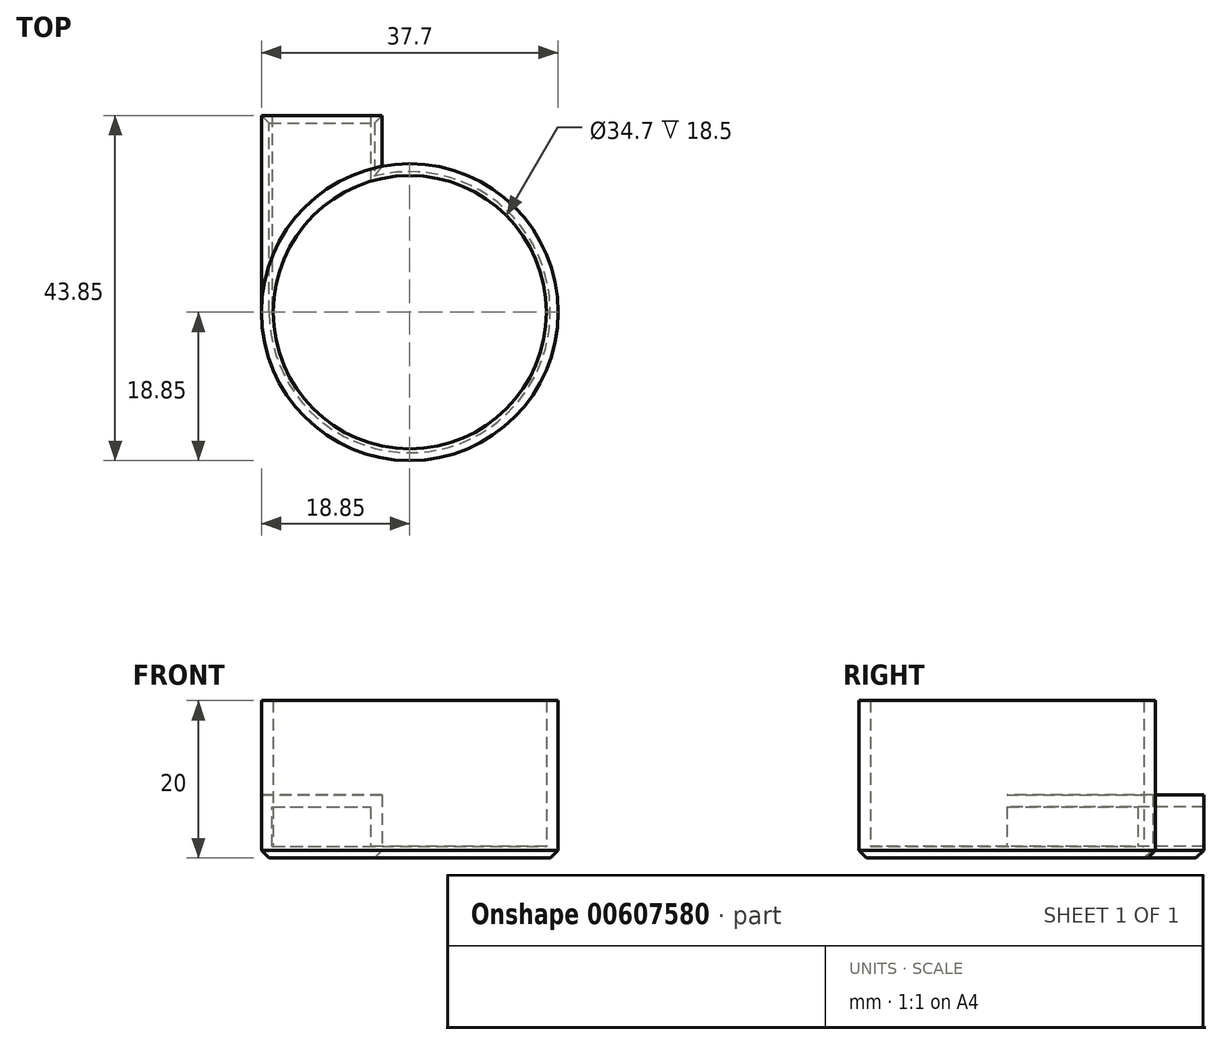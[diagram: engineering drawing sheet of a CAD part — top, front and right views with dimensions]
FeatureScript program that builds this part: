
annotation { "Feature Type Name" : "Feature", "Feature Type Description" : "" }
export const myFeature = defineFeature(function(context is Context, id is Id, definition is map)
    precondition{}
    {
        {
            var Q0;
            Q0=qCreatedBy(makeId("Top.planeOp"),FACE);
            var sketch = newSketch(context, id + "F0", { "sketchPlane" : qUnion([Q0])});
            skCircle(sketch, "E0", {"center": v(0, 0) * mm, "radius": 17.35 * mm});
            skCircle(sketch, "E1.0", {"center": v(0, 0) * mm, "radius": 18.85 * mm});
            skSolve(sketch);
        }
        {
            var Q0;
            Q0=makeQuery(id+"F0.imprint","IMPRINT",FACE,{"disambiguationData":[TD([[makeQuery(id+"F0.imprint","IMPRINT",EDGE,{"derivedFrom":sQuery(id+"F0.wireOp",EDGE,"E0")}),1.0]])]});
            extrude(context, id + "F1", {"entities" : qUnion([Q0]), "depth" : 1.5 * mm, "offsetDistance" : 25 * mm});
        }
        {
            var Q0;
            Q0=makeQuery(id+"F0.imprint","IMPRINT",FACE,{"disambiguationData":[TD([[makeQuery(id+"F0.imprint","IMPRINT",EDGE,{"derivedFrom":sQuery(id+"F0.wireOp",EDGE,"E0")}),-1.0]])]});
            extrude(context, id + "F2", {"entities" : qUnion([Q0]), "operationType" : NewBodyOperationType.ADD, "depth" : 20 * mm, "offsetDistance" : 25 * mm});
        }
        {
            var Q0;
            Q0=qCreatedBy(makeId("Front.planeOp"),FACE);
            var sketch = newSketch(context, id + "F3", { "sketchPlane" : qUnion([Q0])});
            skLineSegment(sketch, "E2.bottom", {"start": v(-17.5, 1.5) * mm, "end": v(-5, 1.5) * mm});
            skLineSegment(sketch, "E2.top", {"start": v(-17.5, 6.5) * mm, "end": v(-5, 6.5) * mm});
            skLineSegment(sketch, "E2.left", {"start": v(-17.5, 1.5) * mm, "end": v(-17.5, 6.5) * mm});
            skLineSegment(sketch, "E3", {"start": v(-5, 6.5) * mm, "end": v(-5, 1.5) * mm});
            skPoint(sketch, "E2.right.end.orphan", {"position": v(0, 6.5) * mm});
            skSolve(sketch);
        }
        {
            var Q0;
            Q0 = qSketchRegion(id + "F3", true);
            extrude(context, id + "F4", {"entities" : qUnion([Q0]), "operationType" : NewBodyOperationType.REMOVE, "oppositeDirection" : true, "depth" : 25 * mm, "offsetDistance" : 25 * mm});
        }
        {
            var Q0;
            Q0=qCreatedBy(makeId("Front.planeOp"),FACE);
            cPlane(context, id + "F5", {"entities" : qUnion([Q0]), "cplaneType" : CPlaneType.OFFSET, "offset" : 25 * mm, "oppositeDirection" : true, "width" : 150 * mm, "height" : 150 * mm});
        }
        {
            var Q0;
            Q0=qCreatedBy(id+"F5.planeOp",FACE);
            var sketch = newSketch(context, id + "F6", { "sketchPlane" : qUnion([Q0])});
            skLineSegment(sketch, "E4.bottom", {"start": v(-17.5, 1.5) * mm, "end": v(-5, 1.5) * mm});
            skLineSegment(sketch, "E4.top", {"start": v(-17.5, 6.5) * mm, "end": v(-5, 6.5) * mm});
            skLineSegment(sketch, "E4.left", {"start": v(-17.5, 1.5) * mm, "end": v(-17.5, 6.5) * mm});
            skLineSegment(sketch, "E5", {"start": v(-5, 6.5) * mm, "end": v(-5, 1.5) * mm});
            skPoint(sketch, "E4.right.end.orphan", {"position": v(9, 6.5) * mm});
            skLineSegment(sketch, "E6.0", {"start": v(-3.5, 8) * mm, "end": v(-3.5, 0) * mm});
            skLineSegment(sketch, "E6.1", {"start": v(-18.85, 8) * mm, "end": v(-3.5, 8) * mm});
            skLineSegment(sketch, "E6.3", {"start": v(-19, 0) * mm, "end": v(-3.5, 0) * mm});
            skLineSegment(sketch, "E7", {"start": v(-18.85, 0) * mm, "end": v(-18.85, 8) * mm});
            skPoint(sketch, "E6.2.end.orphan", {"position": v(-19, 8) * mm});
            skSolve(sketch);
        }
        {
            var Q0;
            Q0=makeQuery(id+"F6.imprint","IMPRINT",FACE,{"disambiguationData":[TD([[makeQuery(id+"F6.imprint","IMPRINT",EDGE,{"derivedFrom":sQuery(id+"F6.wireOp",EDGE,"E4.bottom")}),-1.0]])]});
            var Q1;
            Q1=makeQuery(id+"F2.opExtrude","SWEPT_FACE",FACE,{"disambiguationData":[OSD([sQuery(id+"F0.wireOp",EDGE,"E1.0")])]});
            extrude(context, id + "F7", {"entities" : qUnion([Q0]), "operationType" : NewBodyOperationType.ADD, "endBound" : BoundingType.UP_TO_SURFACE, "depth" : 25 * mm, "endBoundEntityFace" : qUnion([Q1]), "offsetDistance" : 25 * mm});
        }
        {
            var Q0;
            {var subQ0=sQuery(id+"F0.wireOp",EDGE,"E0");Q0=makeQuery(id+"F7.boolean.opBoolean","MERGE",FACE,{"derivedFrom":[makeQuery(id+"F2.boolean.opBoolean","MERGE",FACE,{"derivedFrom":[makeQuery(id+"F1.opExtrude","CAP_FACE",FACE,{"disambiguationData":[OSD([subQ0])],"isStart":true}),makeQuery(id+"F2.opExtrude","CAP_FACE",FACE,{"disambiguationData":[OSD([subQ0,sQuery(id+"F0.wireOp",EDGE,"E1.0")])],"isStart":true})]}),makeQuery(id+"F7.opExtrude","SWEPT_FACE",FACE,{"disambiguationData":[OSD([sQuery(id+"F6.wireOp",EDGE,"E6.3")])]})]});}
            chamfer(context, id + "F8", {"entities" : qUnion([Q0]), "width" : 1 * mm, "tangentPropagation" : true});
        }
    });
